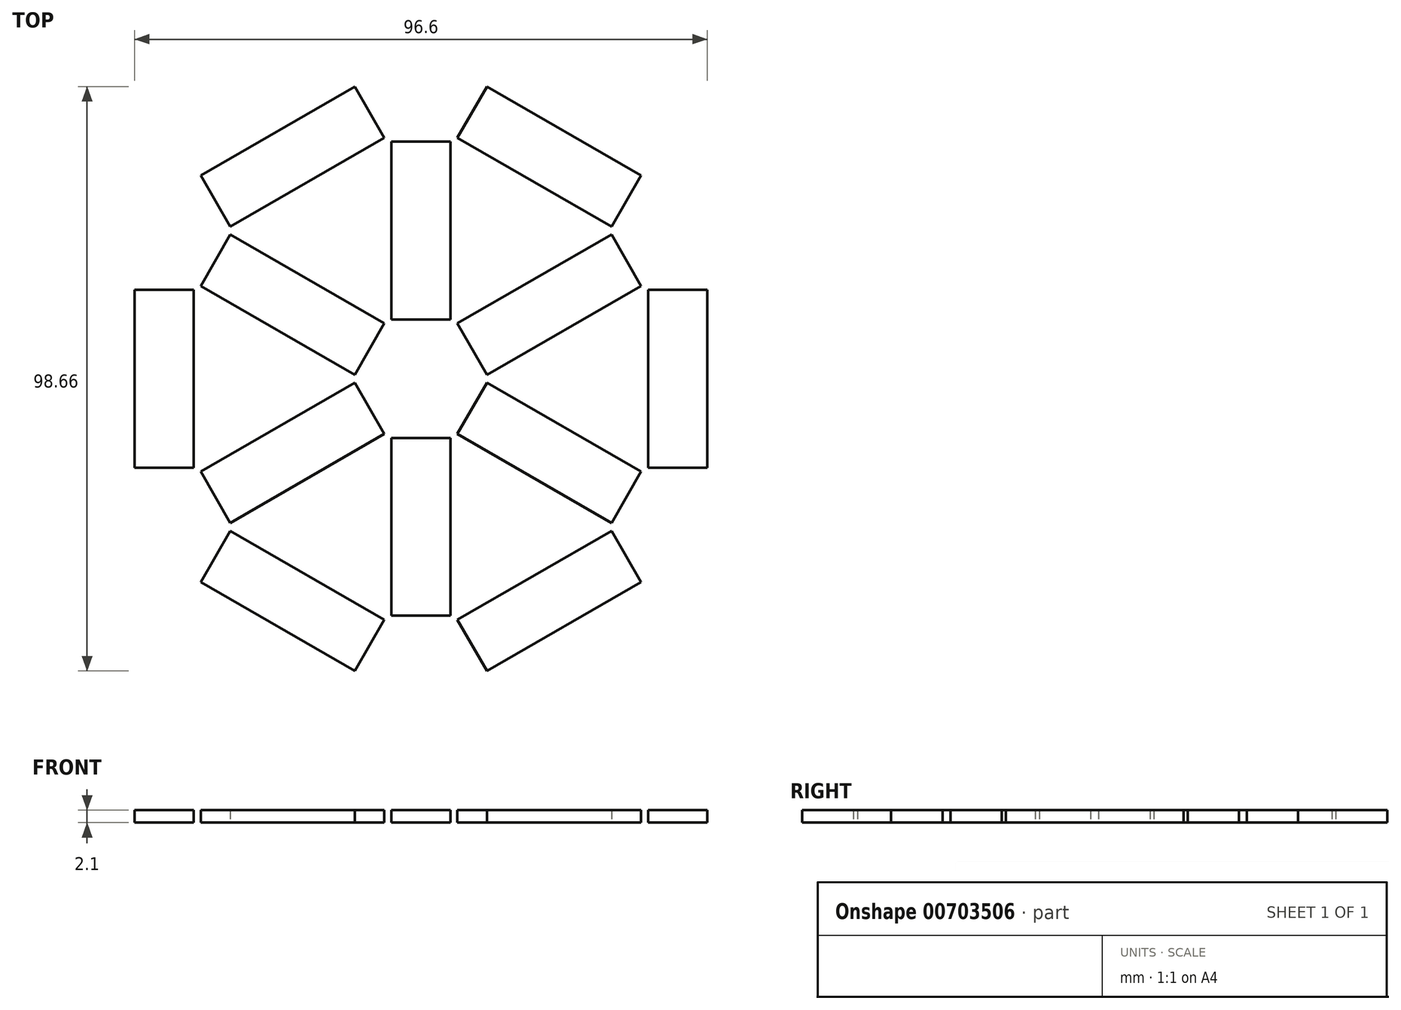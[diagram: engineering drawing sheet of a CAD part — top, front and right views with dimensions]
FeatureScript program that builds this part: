
annotation { "Feature Type Name" : "Feature", "Feature Type Description" : "" }
export const myFeature = defineFeature(function(context is Context, id is Id, definition is map)
    precondition{}
    {
        {
            var Q0;
            Q0=qCreatedBy(makeId("Top.planeOp"),FACE);
            var sketch = newSketch(context, id + "F0", { "sketchPlane" : qUnion([Q0])});
            skLineSegment(sketch, "E0.bottom", {"start": v(-5, 40) * mm, "end": v(5, 40) * mm});
            skLineSegment(sketch, "E0.top", {"start": v(-5, 10) * mm, "end": v(5, 10) * mm});
            skLineSegment(sketch, "E0.left", {"start": v(-5, 40) * mm, "end": v(-5, 10) * mm});
            skLineSegment(sketch, "E0.right", {"start": v(5, 40) * mm, "end": v(5, 10) * mm});
            skLineSegment(sketch, "E1.1.0", {"start": v(-37.14, 15.67) * mm, "end": v(-32.14, 24.33) * mm});
            skLineSegment(sketch, "E1.1.1", {"start": v(-11.16, 0.67) * mm, "end": v(-6.16, 9.33) * mm});
            skLineSegment(sketch, "E1.1.2", {"start": v(-37.14, 15.67) * mm, "end": v(-11.16, 0.67) * mm});
            skLineSegment(sketch, "E1.1.3", {"start": v(-32.14, 24.33) * mm, "end": v(-6.16, 9.33) * mm});
            skLineSegment(sketch, "E1.2.0", {"start": v(-32.14, -24.33) * mm, "end": v(-37.14, -15.67) * mm});
            skLineSegment(sketch, "E1.2.1", {"start": v(-6.16, -9.33) * mm, "end": v(-11.16, -0.67) * mm});
            skLineSegment(sketch, "E1.2.2", {"start": v(-32.14, -24.33) * mm, "end": v(-6.16, -9.33) * mm});
            skLineSegment(sketch, "E1.2.3", {"start": v(-37.14, -15.67) * mm, "end": v(-11.16, -0.67) * mm});
            skLineSegment(sketch, "E1.3.0", {"start": v(5, -40) * mm, "end": v(-5, -40) * mm});
            skLineSegment(sketch, "E1.3.1", {"start": v(5, -10) * mm, "end": v(-5, -10) * mm});
            skLineSegment(sketch, "E1.3.2", {"start": v(5, -40) * mm, "end": v(5, -10) * mm});
            skLineSegment(sketch, "E1.3.3", {"start": v(-5, -40) * mm, "end": v(-5, -10) * mm});
            skLineSegment(sketch, "E1.4.0", {"start": v(37.14, -15.67) * mm, "end": v(32.14, -24.33) * mm});
            skLineSegment(sketch, "E1.4.1", {"start": v(11.16, -0.67) * mm, "end": v(6.16, -9.33) * mm});
            skLineSegment(sketch, "E1.4.2", {"start": v(37.14, -15.67) * mm, "end": v(11.16, -0.67) * mm});
            skLineSegment(sketch, "E1.4.3", {"start": v(32.14, -24.33) * mm, "end": v(6.16, -9.33) * mm});
            skLineSegment(sketch, "E1.5.0", {"start": v(32.14, 24.33) * mm, "end": v(37.14, 15.67) * mm});
            skLineSegment(sketch, "E1.5.1", {"start": v(6.16, 9.33) * mm, "end": v(11.16, 0.67) * mm});
            skLineSegment(sketch, "E1.5.2", {"start": v(32.14, 24.33) * mm, "end": v(6.16, 9.33) * mm});
            skLineSegment(sketch, "E1.5.3", {"start": v(37.14, 15.67) * mm, "end": v(11.16, 0.67) * mm});
            skPoint(sketch, "E1.center", {"position": v(0, 0) * mm});
            skLineSegment(sketch, "E2", {"start": v(-10.2, -32.35) * mm, "end": v(-27.35, -2.63) * mm, "construction": true});
            skLineSegment(sketch, "E3", {"start": v(11.3, -25) * mm, "end": v(-24.7, -25) * mm, "construction": true});
            skLineSegment(sketch, "E4.1.0", {"start": v(-6.16, -40.67) * mm, "end": v(-32.14, -25.67) * mm});
            skLineSegment(sketch, "E4.1.1", {"start": v(-32.14, -25.67) * mm, "end": v(-37.14, -34.33) * mm});
            skLineSegment(sketch, "E4.1.2", {"start": v(-11.16, -49.33) * mm, "end": v(-37.14, -34.33) * mm});
            skLineSegment(sketch, "E4.1.3", {"start": v(-6.16, -40.67) * mm, "end": v(-11.16, -49.33) * mm});
            skPoint(sketch, "E4.center", {"position": v(-14.43, -25) * mm});
            skLineSegment(sketch, "E5.1.0", {"start": v(32.14, -25.67) * mm, "end": v(6.16, -40.67) * mm});
            skLineSegment(sketch, "E5.1.1", {"start": v(32.14, -25.67) * mm, "end": v(37.14, -34.33) * mm});
            skLineSegment(sketch, "E5.1.2", {"start": v(37.14, -34.33) * mm, "end": v(11.16, -49.33) * mm});
            skLineSegment(sketch, "E5.1.3", {"start": v(6.16, -40.67) * mm, "end": v(11.16, -49.33) * mm});
            skLineSegment(sketch, "E5.2.0", {"start": v(38.3, 15) * mm, "end": v(38.3, -15) * mm});
            skLineSegment(sketch, "E5.2.1", {"start": v(38.3, 15) * mm, "end": v(48.3, 15) * mm});
            skLineSegment(sketch, "E5.2.2", {"start": v(48.3, 15) * mm, "end": v(48.3, -15) * mm});
            skLineSegment(sketch, "E5.2.3", {"start": v(38.3, -15) * mm, "end": v(48.3, -15) * mm});
            skLineSegment(sketch, "E5.3.0", {"start": v(6.16, 40.67) * mm, "end": v(32.14, 25.67) * mm});
            skLineSegment(sketch, "E5.3.1", {"start": v(6.16, 40.67) * mm, "end": v(11.16, 49.33) * mm});
            skLineSegment(sketch, "E5.3.2", {"start": v(11.16, 49.33) * mm, "end": v(37.14, 34.33) * mm});
            skLineSegment(sketch, "E5.3.3", {"start": v(32.14, 25.67) * mm, "end": v(37.14, 34.33) * mm});
            skLineSegment(sketch, "E5.4.0", {"start": v(-32.14, 25.67) * mm, "end": v(-6.16, 40.67) * mm});
            skLineSegment(sketch, "E5.4.1", {"start": v(-32.14, 25.67) * mm, "end": v(-37.14, 34.33) * mm});
            skLineSegment(sketch, "E5.4.2", {"start": v(-37.14, 34.33) * mm, "end": v(-11.16, 49.33) * mm});
            skLineSegment(sketch, "E5.4.3", {"start": v(-6.16, 40.67) * mm, "end": v(-11.16, 49.33) * mm});
            skLineSegment(sketch, "E5.5.0", {"start": v(-38.3, -15) * mm, "end": v(-38.3, 15) * mm});
            skLineSegment(sketch, "E5.5.1", {"start": v(-38.3, -15) * mm, "end": v(-48.3, -15) * mm});
            skLineSegment(sketch, "E5.5.2", {"start": v(-48.3, -15) * mm, "end": v(-48.3, 15) * mm});
            skLineSegment(sketch, "E5.5.3", {"start": v(-38.3, 15) * mm, "end": v(-48.3, 15) * mm});
            skSolve(sketch);
        }
        {
            var Q0;
            Q0=makeQuery(id+"F0.imprint","IMPRINT",FACE,{"disambiguationData":[TD([[makeQuery(id+"F0.imprint","IMPRINT",EDGE,{"derivedFrom":sQuery(id+"F0.wireOp",EDGE,"E5.4.0")}),1.0]])]});
            var Q1;
            Q1=makeQuery(id+"F0.imprint","IMPRINT",FACE,{"disambiguationData":[TD([[makeQuery(id+"F0.imprint","IMPRINT",EDGE,{"derivedFrom":sQuery(id+"F0.wireOp",EDGE,"E5.5.0")}),1.0]])]});
            var Q2;
            Q2=makeQuery(id+"F0.imprint","IMPRINT",FACE,{"disambiguationData":[TD([[makeQuery(id+"F0.imprint","IMPRINT",EDGE,{"derivedFrom":sQuery(id+"F0.wireOp",EDGE,"E5.3.0")}),1.0]])]});
            var Q3;
            Q3=makeQuery(id+"F0.imprint","IMPRINT",FACE,{"disambiguationData":[TD([[makeQuery(id+"F0.imprint","IMPRINT",EDGE,{"derivedFrom":sQuery(id+"F0.wireOp",EDGE,"E0.bottom")}),-1.0]])]});
            var Q4;
            Q4=makeQuery(id+"F0.imprint","IMPRINT",FACE,{"disambiguationData":[TD([[makeQuery(id+"F0.imprint","IMPRINT",EDGE,{"derivedFrom":sQuery(id+"F0.wireOp",EDGE,"E5.2.0")}),1.0]])]});
            var Q5;
            Q5=makeQuery(id+"F0.imprint","IMPRINT",FACE,{"disambiguationData":[TD([[makeQuery(id+"F0.imprint","IMPRINT",EDGE,{"derivedFrom":sQuery(id+"F0.wireOp",EDGE,"E1.5.0")}),-1.0]])]});
            var Q6;
            Q6=makeQuery(id+"F0.imprint","IMPRINT",FACE,{"disambiguationData":[TD([[makeQuery(id+"F0.imprint","IMPRINT",EDGE,{"derivedFrom":sQuery(id+"F0.wireOp",EDGE,"E1.1.0")}),-1.0]])]});
            var Q7;
            Q7=makeQuery(id+"F0.imprint","IMPRINT",FACE,{"disambiguationData":[TD([[makeQuery(id+"F0.imprint","IMPRINT",EDGE,{"derivedFrom":sQuery(id+"F0.wireOp",EDGE,"E1.4.0")}),-1.0]])]});
            var Q8;
            Q8=makeQuery(id+"F0.imprint","IMPRINT",FACE,{"disambiguationData":[TD([[makeQuery(id+"F0.imprint","IMPRINT",EDGE,{"derivedFrom":sQuery(id+"F0.wireOp",EDGE,"E5.1.0")}),1.0]])]});
            var Q9;
            Q9=makeQuery(id+"F0.imprint","IMPRINT",FACE,{"disambiguationData":[TD([[makeQuery(id+"F0.imprint","IMPRINT",EDGE,{"derivedFrom":sQuery(id+"F0.wireOp",EDGE,"E1.3.0")}),-1.0]])]});
            var Q10;
            Q10=makeQuery(id+"F0.imprint","IMPRINT",FACE,{"disambiguationData":[TD([[makeQuery(id+"F0.imprint","IMPRINT",EDGE,{"derivedFrom":sQuery(id+"F0.wireOp",EDGE,"E1.2.0")}),-1.0]])]});
            var Q11;
            Q11=makeQuery(id+"F0.imprint","IMPRINT",FACE,{"disambiguationData":[TD([[makeQuery(id+"F0.imprint","IMPRINT",EDGE,{"derivedFrom":sQuery(id+"F0.wireOp",EDGE,"E4.1.0")}),1.0]])]});
            extrude(context, id + "F1", {"entities" : qUnion([Q0, Q1, Q2, Q3, Q4, Q5, Q6, Q7, Q8, Q9, Q10, Q11]), "depth" : 2.1 * mm, "offsetDistance" : 25 * mm});
        }
    });
